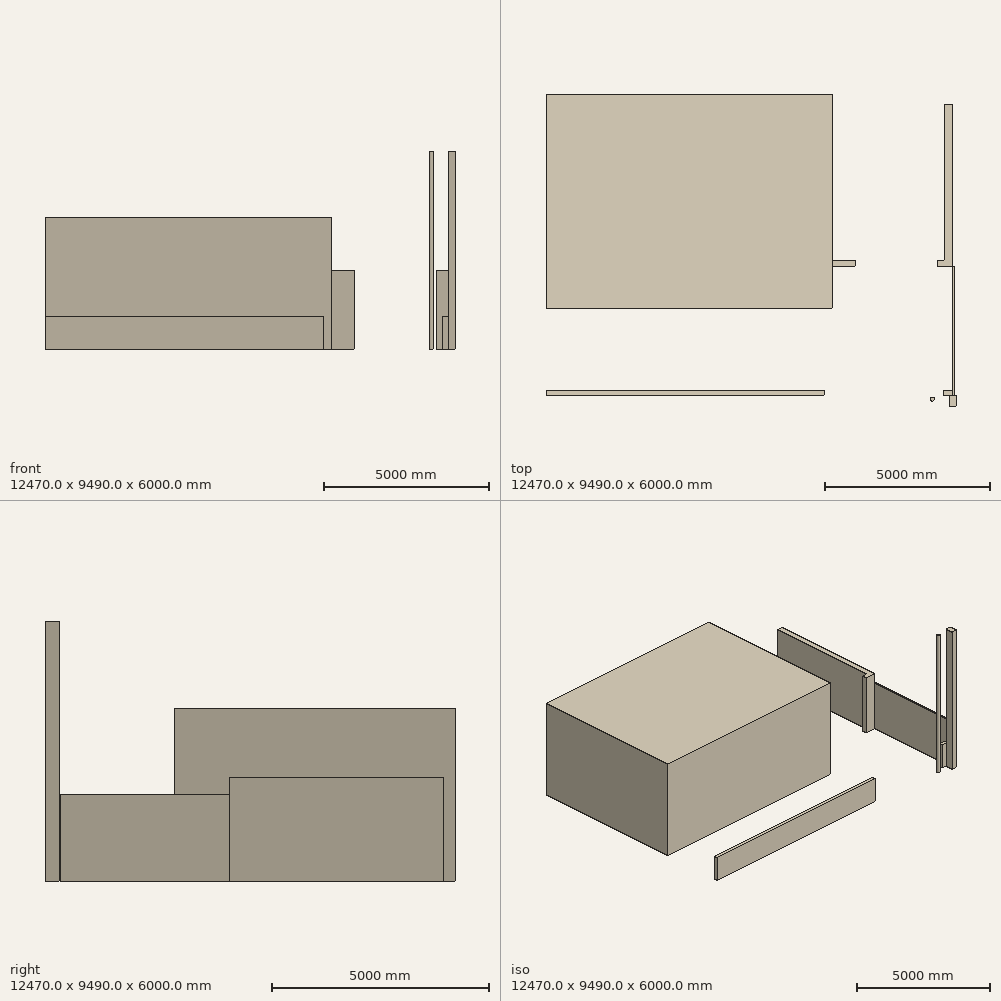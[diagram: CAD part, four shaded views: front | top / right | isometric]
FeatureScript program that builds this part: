
annotation { "Feature Type Name" : "Feature", "Feature Type Description" : "" }
export const myFeature = defineFeature(function(context is Context, id is Id, definition is map)
    precondition{}
    {
        {
            var Q0;
            Q0=qCreatedBy(makeId("Top.planeOp"),FACE);
            var sketch = newSketch(context, id + "F0", { "sketchPlane" : qUnion([Q0])});
            skLineSegment(sketch, "E0.bottom", {"start": v(-100, -20) * mm, "end": v(120, -20) * mm});
            skLineSegment(sketch, "E0.top", {"start": v(-100, -340) * mm, "end": v(120, -340) * mm});
            skLineSegment(sketch, "E0.left", {"start": v(-100, -20) * mm, "end": v(-100, -340) * mm});
            skLineSegment(sketch, "E0.right", {"start": v(120, -20) * mm, "end": v(120, -340) * mm});
            skLineSegment(sketch, "E1.bottom", {"start": v(0, 0) * mm, "end": v(-290, 0) * mm});
            skLineSegment(sketch, "E1.top", {"start": v(0, 150) * mm, "end": v(-290, 150) * mm});
            skLineSegment(sketch, "E1.left", {"start": v(0, 0) * mm, "end": v(0, 150) * mm});
            skLineSegment(sketch, "E1.right", {"start": v(-290, 0) * mm, "end": v(-290, 150) * mm});
            skLineSegment(sketch, "E2.bottom", {"start": v(0, 0) * mm, "end": v(50, 0) * mm});
            skLineSegment(sketch, "E2.left", {"start": v(0, 0) * mm, "end": v(0, 2650) * mm});
            skLineSegment(sketch, "E2.right", {"start": v(50, 0) * mm, "end": v(50, 3920) * mm});
            skArc(sketch, "E3", {"start": v(-550, -103.64) * mm, "mid": v(-679, -115) * mm, "end": v(-550, -126.36) * mm});
            skLineSegment(sketch, "E4", {"start": v(-3640, 2650) * mm, "end": v(-12350, 2650) * mm});
            skLineSegment(sketch, "E5.bottom", {"start": v(-3890, 0) * mm, "end": v(-12350, 0) * mm});
            skLineSegment(sketch, "E5.top", {"start": v(-3890, 150) * mm, "end": v(-12350, 150) * mm});
            skLineSegment(sketch, "E5.left", {"start": v(-3890, 0) * mm, "end": v(-3890, 150) * mm});
            skLineSegment(sketch, "E5.right", {"start": v(-12350, 0) * mm, "end": v(-12350, 150) * mm});
            skLineSegment(sketch, "E6", {"start": v(0, 2650) * mm, "end": v(0, 9150) * mm});
            skLineSegment(sketch, "E7", {"start": v(0, 9150) * mm, "end": v(-12350, 9150) * mm});
            skLineSegment(sketch, "E8", {"start": v(-12350, 9150) * mm, "end": v(-12350, 2650) * mm});
            skLineSegment(sketch, "E9", {"start": v(-3640, 2650) * mm, "end": v(-3640, 3920) * mm});
            skLineSegment(sketch, "E10", {"start": v(-3640, 3920) * mm, "end": v(0, 3920) * mm});
            skLineSegment(sketch, "E11", {"start": v(-3640, 3920) * mm, "end": v(-3640, 9150) * mm});
            skLineSegment(sketch, "E12", {"start": v(-3640, 4110) * mm, "end": v(-2950, 4110) * mm});
            skLineSegment(sketch, "E13", {"start": v(-2950, 4110) * mm, "end": v(-2950, 3920) * mm});
            skLineSegment(sketch, "E14", {"start": v(-210, 3920) * mm, "end": v(-210, 4110) * mm});
            skLineSegment(sketch, "E15", {"start": v(-210, 4110) * mm, "end": v(0, 4110) * mm});
            skLineSegment(sketch, "E16", {"start": v(-12350, 150) * mm, "end": v(-12350, 2650) * mm});
            skLineSegment(sketch, "E17", {"start": v(-12200, 2650) * mm, "end": v(-12200, 150) * mm});
            skLineSegment(sketch, "E18", {"start": v(0, 3920) * mm, "end": v(50, 3920) * mm});
            skLineSegment(sketch, "E19", {"start": v(-550, -103.64) * mm, "end": v(-550, -126.36) * mm});
            skSolve(sketch);
        }
        {
            var Q0;
            Q0=makeQuery(id+"F0.imprint","IMPRINT",FACE,{"disambiguationData":[TD([[makeQuery(id+"F0.imprint","IMPRINT",EDGE,{"derivedFrom":sQuery(id+"F0.wireOp",EDGE,"E3")}),1.0]])]});
            var Q1;
            Q1=makeQuery(id+"F0.imprint","IMPRINT",FACE,{"disambiguationData":[TD([[makeQuery(id+"F0.imprint","IMPRINT",EDGE,{"derivedFrom":sQuery(id+"F0.wireOp",EDGE,"E0.bottom")}),-1.0]])]});
            extrude(context, id + "F1", {"entities" : qUnion([Q0, Q1]), "depth" : 6000 * mm});
        }
        {
            var Q0;
            Q0=makeQuery(id+"F0.imprint","IMPRINT",FACE,{"disambiguationData":[TD([[makeQuery(id+"F0.imprint","IMPRINT",EDGE,{"derivedFrom":sQuery(id+"F0.wireOp",EDGE,"E5.bottom")}),-1.0]])]});
            var Q1;
            {var subQ0=sQuery(id+"F0.wireOp",EDGE,"E1.bottom");Q1=makeQuery(id+"F0.imprint","IMPRINT",FACE,{"disambiguationData":[TD([[makeQuery(id+"F0.imprint","IMPRINT",EDGE,{"derivedFrom":subQ0}),-1.0]])]});}
            extrude(context, id + "F2", {"entities" : qUnion([Q0, Q1]), "depth" : 1000 * mm});
        }
        {
            var Q0;
            {var subQ3=sQuery(id+"F0.wireOp",EDGE,"E2.bottom");Q0=makeQuery(id+"F0.imprint","IMPRINT",FACE,{"disambiguationData":[TD([[makeQuery(id+"F0.imprint","IMPRINT",EDGE,{"derivedFrom":subQ3}),1.0]])]});}
            extrude(context, id + "F3", {"entities" : qUnion([Q0]), "operationType" : NewBodyOperationType.ADD, "depth" : 2000 * mm});
        }
        {
            var Q0;
            Q0=makeQuery(id+"F0.imprint","IMPRINT",FACE,{"disambiguationData":[TD([[makeQuery(id+"F0.imprint","IMPRINT",EDGE,{"derivedFrom":sQuery(id+"F0.wireOp",EDGE,"E4")}),-1.0]])]});
            extrude(context, id + "F4", {"entities" : qUnion([Q0]), "depth" : 4000 * mm});
        }
        {
            var Q0;
            Q0=qCreatedBy(makeId("Top.planeOp"),FACE);
            var sketch = newSketch(context, id + "F5", { "sketchPlane" : qUnion([Q0])});
            skLineSegment(sketch, "E20.bottom", {"start": v(-2950, 3920) * mm, "end": v(-3640, 3920) * mm});
            skLineSegment(sketch, "E20.top", {"start": v(-2950, 4110) * mm, "end": v(-3640, 4110) * mm});
            skLineSegment(sketch, "E20.left", {"start": v(-2950, 3920) * mm, "end": v(-2950, 4110) * mm});
            skLineSegment(sketch, "E20.right", {"start": v(-3640, 3920) * mm, "end": v(-3640, 4110) * mm});
            skLineSegment(sketch, "E21.bottom", {"start": v(-450, 3920) * mm, "end": v(0, 3920) * mm});
            skLineSegment(sketch, "E21.top", {"start": v(-450, 4110) * mm, "end": v(0, 4110) * mm});
            skLineSegment(sketch, "E21.left", {"start": v(-450, 3920) * mm, "end": v(-450, 4110) * mm});
            skLineSegment(sketch, "E21.right", {"start": v(0, 3920) * mm, "end": v(0, 4110) * mm});
            skLineSegment(sketch, "E22.bottom", {"start": v(0, 8860.26) * mm, "end": v(-240, 8860.26) * mm});
            skLineSegment(sketch, "E22.top", {"start": v(0, 4110) * mm, "end": v(-240, 4110) * mm});
            skLineSegment(sketch, "E22.left", {"start": v(0, 8860.26) * mm, "end": v(0, 4110) * mm});
            skLineSegment(sketch, "E22.right", {"start": v(-240, 8860.26) * mm, "end": v(-240, 4110) * mm});
            skSolve(sketch);
        }
        {
            var Q0;
            Q0=makeQuery(id+"F5.imprint","IMPRINT",FACE,{"disambiguationData":[TD([[makeQuery(id+"F5.imprint","IMPRINT",EDGE,{"derivedFrom":sQuery(id+"F5.wireOp",EDGE,"E20.bottom")}),-1.0]])]});
            var Q1;
            Q1=makeQuery(id+"F5.imprint","IMPRINT",FACE,{"disambiguationData":[TD([[makeQuery(id+"F5.imprint","IMPRINT",EDGE,{"derivedFrom":sQuery(id+"F5.wireOp",EDGE,"E21.bottom")}),1.0]])]});
            var Q2;
            Q2=makeQuery(id+"F5.imprint","IMPRINT",FACE,{"disambiguationData":[TD([[makeQuery(id+"F5.imprint","IMPRINT",EDGE,{"derivedFrom":sQuery(id+"F5.wireOp",EDGE,"E22.bottom")}),1.0]])]});
            extrude(context, id + "F6", {"entities" : qUnion([Q0, Q1, Q2]), "operationType" : NewBodyOperationType.ADD, "depth" : 2400 * mm});
        }
    });
